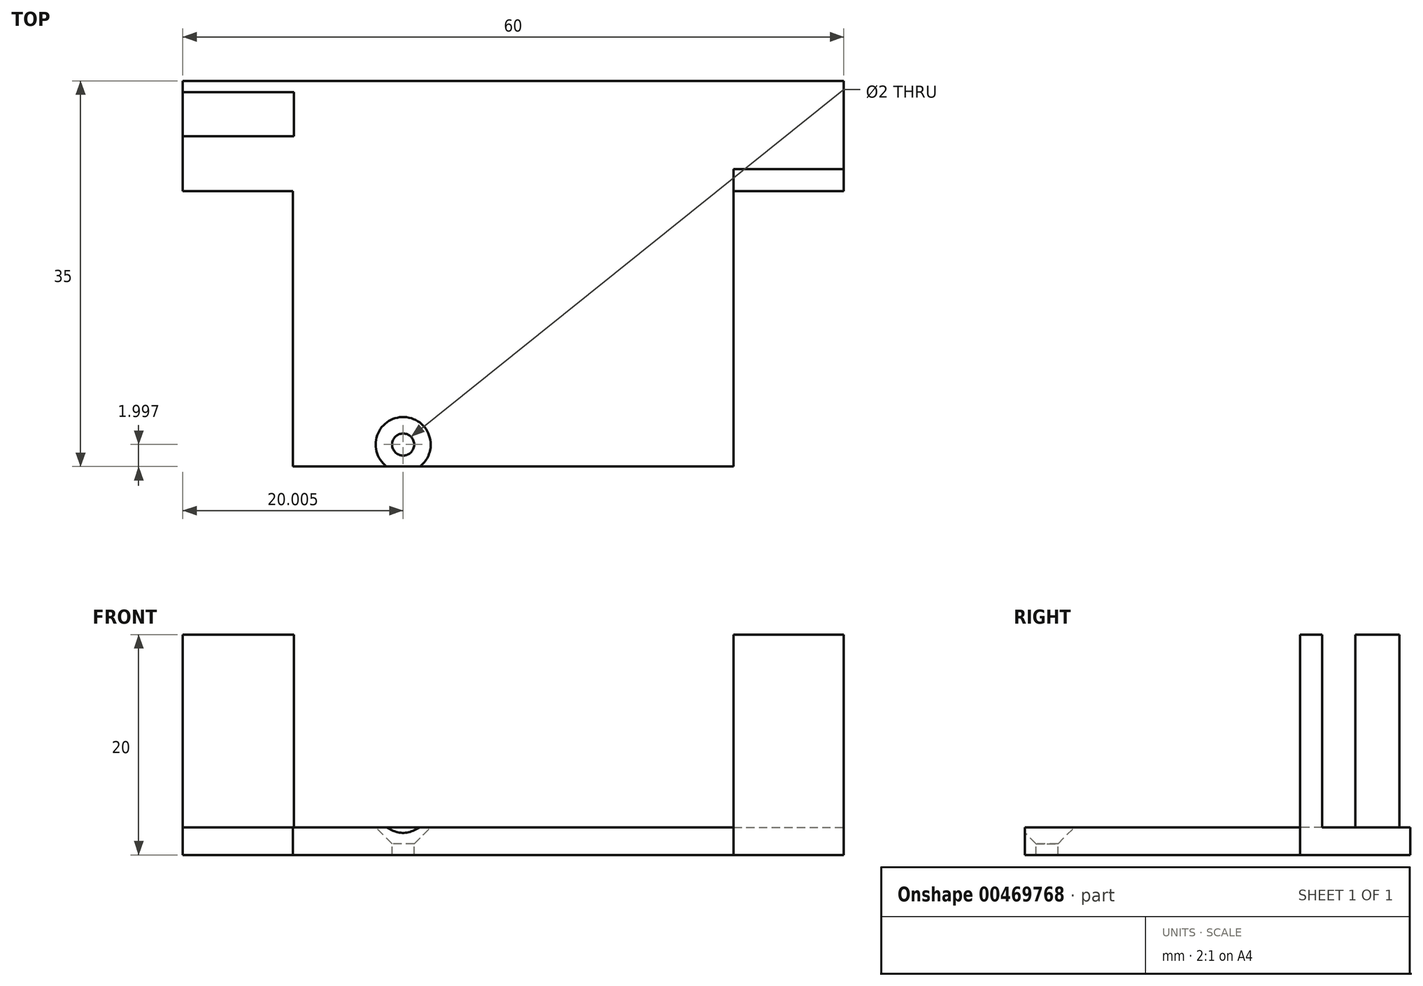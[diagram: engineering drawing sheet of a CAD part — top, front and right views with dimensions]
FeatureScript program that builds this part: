
annotation { "Feature Type Name" : "Feature", "Feature Type Description" : "" }
export const myFeature = defineFeature(function(context is Context, id is Id, definition is map)
    precondition{}
    {
        {
            var Q0;
            Q0=qCreatedBy(makeId("Top.planeOp"),FACE);
            var sketch = newSketch(context, id + "F0", { "sketchPlane" : qUnion([Q0])});
            skLineSegment(sketch, "E0.bottom", {"start": v(-30.63, 18.73) * mm, "end": v(9.37, 18.73) * mm});
            skLineSegment(sketch, "E0.top", {"start": v(-30.63, -6.27) * mm, "end": v(9.37, -6.27) * mm});
            skLineSegment(sketch, "E0.left", {"start": v(-30.63, 18.73) * mm, "end": v(-30.63, -6.27) * mm});
            skLineSegment(sketch, "E0.right", {"start": v(9.37, 18.73) * mm, "end": v(9.37, -6.27) * mm});
            skLineSegment(sketch, "E1.bottom", {"start": v(-40.63, 28.73) * mm, "end": v(19.37, 28.73) * mm});
            skLineSegment(sketch, "E1.top", {"start": v(-40.63, 18.73) * mm, "end": v(19.37, 18.73) * mm});
            skLineSegment(sketch, "E1.left", {"start": v(-40.63, 28.73) * mm, "end": v(-40.63, 18.73) * mm});
            skLineSegment(sketch, "E1.right", {"start": v(19.37, 28.73) * mm, "end": v(19.37, 18.73) * mm});
            skLineSegment(sketch, "E2", {"start": v(9.37, 18.73) * mm, "end": v(9.37, 20.73) * mm});
            skLineSegment(sketch, "E3", {"start": v(9.37, 20.73) * mm, "end": v(19.37, 20.73) * mm});
            skLineSegment(sketch, "E4", {"start": v(-40.63, 23.73) * mm, "end": v(-30.55, 23.73) * mm});
            skLineSegment(sketch, "E5", {"start": v(-30.55, 23.73) * mm, "end": v(-30.55, 27.73) * mm});
            skLineSegment(sketch, "E6", {"start": v(-30.55, 27.73) * mm, "end": v(-40.63, 27.73) * mm});
            skLineSegment(sketch, "E7.bottom", {"start": v(19.37, 18.73) * mm, "end": v(19.37, 18.73) * mm});
            skLineSegment(sketch, "E7.top", {"start": v(19.37, 16.73) * mm, "end": v(19.37, 16.73) * mm});
            skLineSegment(sketch, "E7.left", {"start": v(19.37, 18.73) * mm, "end": v(19.37, 16.73) * mm});
            skLineSegment(sketch, "E7.right", {"start": v(19.37, 18.73) * mm, "end": v(19.37, 16.73) * mm});
            skLineSegment(sketch, "E8.bottom", {"start": v(9.37, 16.73) * mm, "end": v(9.37, 16.73) * mm});
            skLineSegment(sketch, "E8.top", {"start": v(9.37, 18.73) * mm, "end": v(9.37, 18.73) * mm});
            skLineSegment(sketch, "E8.left", {"start": v(9.37, 16.73) * mm, "end": v(9.37, 18.73) * mm});
            skLineSegment(sketch, "E8.right", {"start": v(9.37, 16.73) * mm, "end": v(9.37, 18.73) * mm});
            skLineSegment(sketch, "E9", {"start": v(19.37, 16.73) * mm, "end": v(9.37, 16.73) * mm});
            skPoint(sketch, "E10", {"position": v(-20.63, -4.27) * mm});
            skSolve(sketch);
        }
        {
            var Q0;
            Q0=makeQuery(id+"F0.imprint","IMPRINT",FACE,{"disambiguationData":[TD([[makeQuery(id+"F0.imprint","IMPRINT",EDGE,{"derivedFrom":sQuery(id+"F0.wireOp",EDGE,"E0.top")}),1.0]])]});
            var Q1;
            {var subQ3=sQuery(id+"F0.wireOp",EDGE,"E1.bottom");Q1=makeQuery(id+"F0.imprint","IMPRINT",FACE,{"disambiguationData":[TD([[makeQuery(id+"F0.imprint","IMPRINT",EDGE,{"derivedFrom":subQ3}),-1.0]])]});}
            extrude(context, id + "F1", {"entities" : qUnion([Q0, Q1]), "depth" : 2.5 * mm});
        }
        {
            var Q0;
            {var subQ0=sQuery(id+"F0.wireOp",EDGE,"E4");Q0=makeQuery(id+"F0.imprint","IMPRINT",FACE,{"disambiguationData":[TD([[makeQuery(id+"F0.imprint","IMPRINT",EDGE,{"derivedFrom":subQ0}),1.0]])]});}
            var Q1;
            {var subQ0=sQuery(id+"F0.wireOp",EDGE,"E2");Q1=makeQuery(id+"F0.imprint","IMPRINT",FACE,{"disambiguationData":[TD([[makeQuery(id+"F0.imprint","IMPRINT",EDGE,{"derivedFrom":subQ0}),-1.0]])]});}
            var Q2;
            {var subQ0=sQuery(id+"F0.wireOp",EDGE,"E7.right");Q2=makeQuery(id+"F0.imprint","IMPRINT",FACE,{"disambiguationData":[TD([[makeQuery(id+"F0.imprint","IMPRINT",EDGE,{"derivedFrom":subQ0}),-1.0]])]});}
            extrude(context, id + "F2", {"entities" : qUnion([Q0, Q1, Q2]), "operationType" : NewBodyOperationType.ADD, "depth" : 20 * mm});
        }
        {
            var Q0;
            Q0=makeQuery(id+"F1.opExtrude","CAP_FACE",FACE,{"disambiguationData":[OSD([sQuery(id+"F0.wireOp",EDGE,"E0.top"),sQuery(id+"F0.wireOp",EDGE,"E0.left"),sQuery(id+"F0.wireOp",EDGE,"E0.right"),sQuery(id+"F0.wireOp",EDGE,"E1.bottom"),sQuery(id+"F0.wireOp",EDGE,"E1.top"),sQuery(id+"F0.wireOp",EDGE,"E1.left"),sQuery(id+"F0.wireOp",EDGE,"E1.right"),sQuery(id+"F0.wireOp",EDGE,"E2"),sQuery(id+"F0.wireOp",EDGE,"E3"),sQuery(id+"F0.wireOp",EDGE,"E4"),sQuery(id+"F0.wireOp",EDGE,"E5"),sQuery(id+"F0.wireOp",EDGE,"E6"),sQuery(id+"F0.wireOp",EDGE,"E8.right")])],"isStart":false});
            var sketch = newSketch(context, id + "F3", { "sketchPlane" : qUnion([Q0])});
            skPoint(sketch, "E11.0", {"position": v(-20.63, -4.27) * mm});
            skSolve(sketch);
        }
        {
            var Q0;
            Q0=sQuery(id+"F3.wireOp",VERTEX,"E11.0");
            var Q1;
            Q1=makeQuery(id+"F1.opExtrude","SWEPT_BODY",BODY,{"disambiguationData":[OSD([sQuery(id+"F0.wireOp",EDGE,"E0.top"),sQuery(id+"F0.wireOp",EDGE,"E0.left"),sQuery(id+"F0.wireOp",EDGE,"E0.right"),sQuery(id+"F0.wireOp",EDGE,"E1.bottom"),sQuery(id+"F0.wireOp",EDGE,"E1.top"),sQuery(id+"F0.wireOp",EDGE,"E1.left"),sQuery(id+"F0.wireOp",EDGE,"E1.right"),sQuery(id+"F0.wireOp",EDGE,"E2"),sQuery(id+"F0.wireOp",EDGE,"E3"),sQuery(id+"F0.wireOp",EDGE,"E4"),sQuery(id+"F0.wireOp",EDGE,"E5"),sQuery(id+"F0.wireOp",EDGE,"E6"),sQuery(id+"F0.wireOp",EDGE,"E8.right")])]});
            hole(context, id + "F4", {"style" : HoleStyle.C_SINK, "endStyle" : HoleEndStyle.THROUGH, "holeDiameter" : 2 * mm, "cSinkDiameter" : 5 * mm, "cSinkAngle" : 90 * degree, "isTappedThrough" : true, "tappedDepth" : 12 * mm, "tapClearance" : 3, "locations" : qUnion([Q0]), "scope" : qUnion([Q1])});
        }
    });
